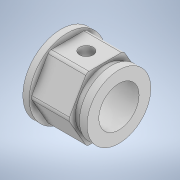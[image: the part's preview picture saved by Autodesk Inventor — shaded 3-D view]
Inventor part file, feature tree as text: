
AUTODESK INVENTOR PART (.ipt)
format: ipt  version: 2020 (Build 240168000, 168)  size: 172,544 bytes
history: native  units: mm
features: sketch x9, extrude x7, fillet x2
ambient origin geometry x8: Origin, YZ Plane, XZ Plane, XY Plane, X Axis, Y Axis, Z Axis, Center Point
bodies: Solid1 (feature_tree)
feature tree (18):
  extrude  "Extrusion1"  Depth=1.28mm TaperAngle=0.0deg
  extrude  "Extrusion2"  Depth=11.854mm
  extrude  "Extrusion3"  Depth=1.5mm TaperAngle=0.0deg
  extrude  "Extrusion4"  Depth=0.75mm
  fillet  "Fillet1"  Radius=2.705mm
  fillet  "Fillet2"  Radius=6.5mm
  sketch  "Sketch5"  dims[d15=6.4mm d16=11.75mm d17=0.0mm]
  extrude  "Extrusion5"  Depth=11.75mm TaperAngle=0.0deg
  sketch  "Sketch7"
  sketch  "Sketch8"
  extrude  "Extrusion6"  Depth=13.75mm TaperAngle=0.0deg
  extrude  "Extrusion7"  [1 undecoded]
  sketch  "Sketch1"  dims[d0=15.197mm d1=1.28mm d2=0.0mm]
  sketch  "Sketch2"  dims[d3=7.5mm d4=0.0mm d5=11.854mm]
  sketch  "Sketch3"  dims[d6=1.22mm d7=0.0mm d8=1.5mm d9=0.0mm]
  sketch  "Sketch4"  dims[d10=0.75mm d11=0.75mm d12=2.705mm d13=6.5mm d14=0.0mm]
  sketch  "Sketch6"  dims[d18=8.0mm d19=13.75mm d20=0.0mm]
  sketch  "Sketch9"
note: 1 required parameter value undecoded (feature->parameter linkage not recoverable at this tier; creation-order binding heuristic only, values carry confidence <= 0.55)
